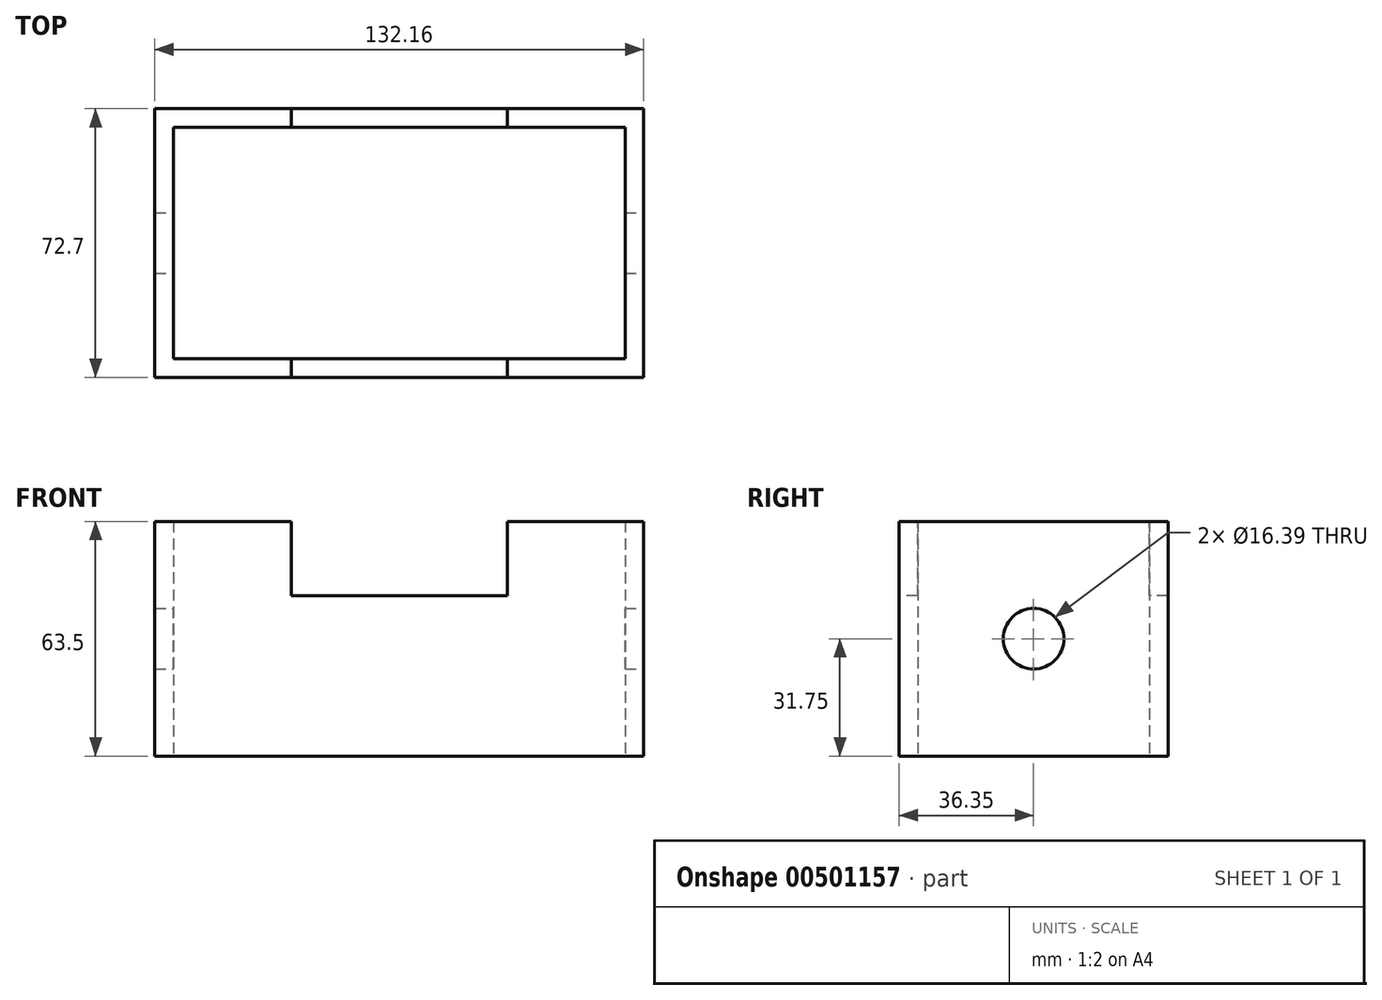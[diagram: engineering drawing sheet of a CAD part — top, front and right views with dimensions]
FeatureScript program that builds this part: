
annotation { "Feature Type Name" : "Feature", "Feature Type Description" : "" }
export const myFeature = defineFeature(function(context is Context, id is Id, definition is map)
    precondition{}
    {
        {
            var Q0;
            Q0=qCreatedBy(makeId("Top.planeOp"),FACE);
            var sketch = newSketch(context, id + "F0", { "sketchPlane" : qUnion([Q0])});
            skLineSegment(sketch, "E0.bottom", {"start": v(-66.08, 36.35) * mm, "end": v(66.08, 36.35) * mm});
            skLineSegment(sketch, "E0.top", {"start": v(-66.08, -36.35) * mm, "end": v(66.08, -36.35) * mm});
            skLineSegment(sketch, "E0.left", {"start": v(-66.08, 36.35) * mm, "end": v(-66.08, -36.35) * mm});
            skLineSegment(sketch, "E0.right", {"start": v(66.08, 36.35) * mm, "end": v(66.08, -36.35) * mm});
            skPoint(sketch, "E0.middle", {"position": v(0, 0) * mm});
            skLineSegment(sketch, "E1.0", {"start": v(-61.08, 31.35) * mm, "end": v(61.08, 31.35) * mm});
            skLineSegment(sketch, "E1.1", {"start": v(-61.08, 31.35) * mm, "end": v(-61.08, -31.35) * mm});
            skLineSegment(sketch, "E1.2", {"start": v(-61.08, -31.35) * mm, "end": v(61.08, -31.35) * mm});
            skLineSegment(sketch, "E1.3", {"start": v(61.08, 31.35) * mm, "end": v(61.08, -31.35) * mm});
            skSolve(sketch);
        }
        {
            var Q0;
            Q0=makeQuery(id+"F0.imprint","IMPRINT",FACE,{"disambiguationData":[TD([[makeQuery(id+"F0.imprint","IMPRINT",EDGE,{"derivedFrom":sQuery(id+"F0.wireOp",EDGE,"E0.bottom")}),-1.0]])]});
            extrude(context, id + "F1", {"entities" : qUnion([Q0]), "depth" : 63.5 * mm});
        }
        {
            var Q0;
            Q0=makeQuery(id+"F1.opExtrude","SWEPT_FACE",FACE,{"disambiguationData":[OSD([sQuery(id+"F0.wireOp",EDGE,"E0.right")])]});
            var sketch = newSketch(context, id + "F2", { "sketchPlane" : qUnion([Q0])});
            skCircle(sketch, "E2", {"center": v(0, 31.75) * mm, "radius": 8.2 * mm});
            skPoint(sketch, "E2.centerSnap0", {"position": v(36.35, 31.75) * mm});
            skPoint(sketch, "E2.centerSnap1", {"position": v(0, 63.5) * mm});
            skSolve(sketch);
        }
        {
            var Q0;
            Q0=makeQuery(id+"F2.imprint","IMPRINT",FACE,{"disambiguationData":[TD([[makeQuery(id+"F2.imprint","IMPRINT",EDGE,{"derivedFrom":sQuery(id+"F2.wireOp",EDGE,"E2")}),1.0]])]});
            extrude(context, id + "F3", {"entities" : qUnion([Q0]), "operationType" : NewBodyOperationType.REMOVE, "endBound" : BoundingType.THROUGH_ALL, "oppositeDirection" : true, "depth" : 25 * mm});
        }
        {
            var Q0;
            Q0=makeQuery(id+"F1.opExtrude","SWEPT_FACE",FACE,{"disambiguationData":[OSD([sQuery(id+"F0.wireOp",EDGE,"E0.top")])]});
            var sketch = newSketch(context, id + "F4", { "sketchPlane" : qUnion([Q0])});
            skLineSegment(sketch, "E3.bottom", {"start": v(-29.24, 67.5) * mm, "end": v(29.24, 67.5) * mm});
            skLineSegment(sketch, "E3.top", {"start": v(-29.24, 43.44) * mm, "end": v(29.24, 43.44) * mm});
            skLineSegment(sketch, "E3.left", {"start": v(-29.24, 67.5) * mm, "end": v(-29.24, 43.44) * mm});
            skLineSegment(sketch, "E3.right", {"start": v(29.24, 67.5) * mm, "end": v(29.24, 43.44) * mm});
            skPoint(sketch, "E3.middle", {"position": v(0, 55.47) * mm});
            skPoint(sketch, "E3.middle.positionSnap0", {"position": v(0, 0) * mm});
            skPoint(sketch, "E3.centerSnap0", {"position": v(0, 0) * mm});
            skSolve(sketch);
        }
        {
            var Q0;
            {var subQ0=sQuery(id+"F4.wireOp",EDGE,"E3.top");Q0=makeQuery(id+"F4.imprint","IMPRINT",FACE,{"disambiguationData":[TD([[makeQuery(id+"F4.imprint","IMPRINT",EDGE,{"derivedFrom":subQ0}),1.0]])]});}
            extrude(context, id + "F5", {"entities" : qUnion([Q0]), "operationType" : NewBodyOperationType.REMOVE, "endBound" : BoundingType.THROUGH_ALL, "oppositeDirection" : true, "depth" : 25 * mm});
        }
    });
